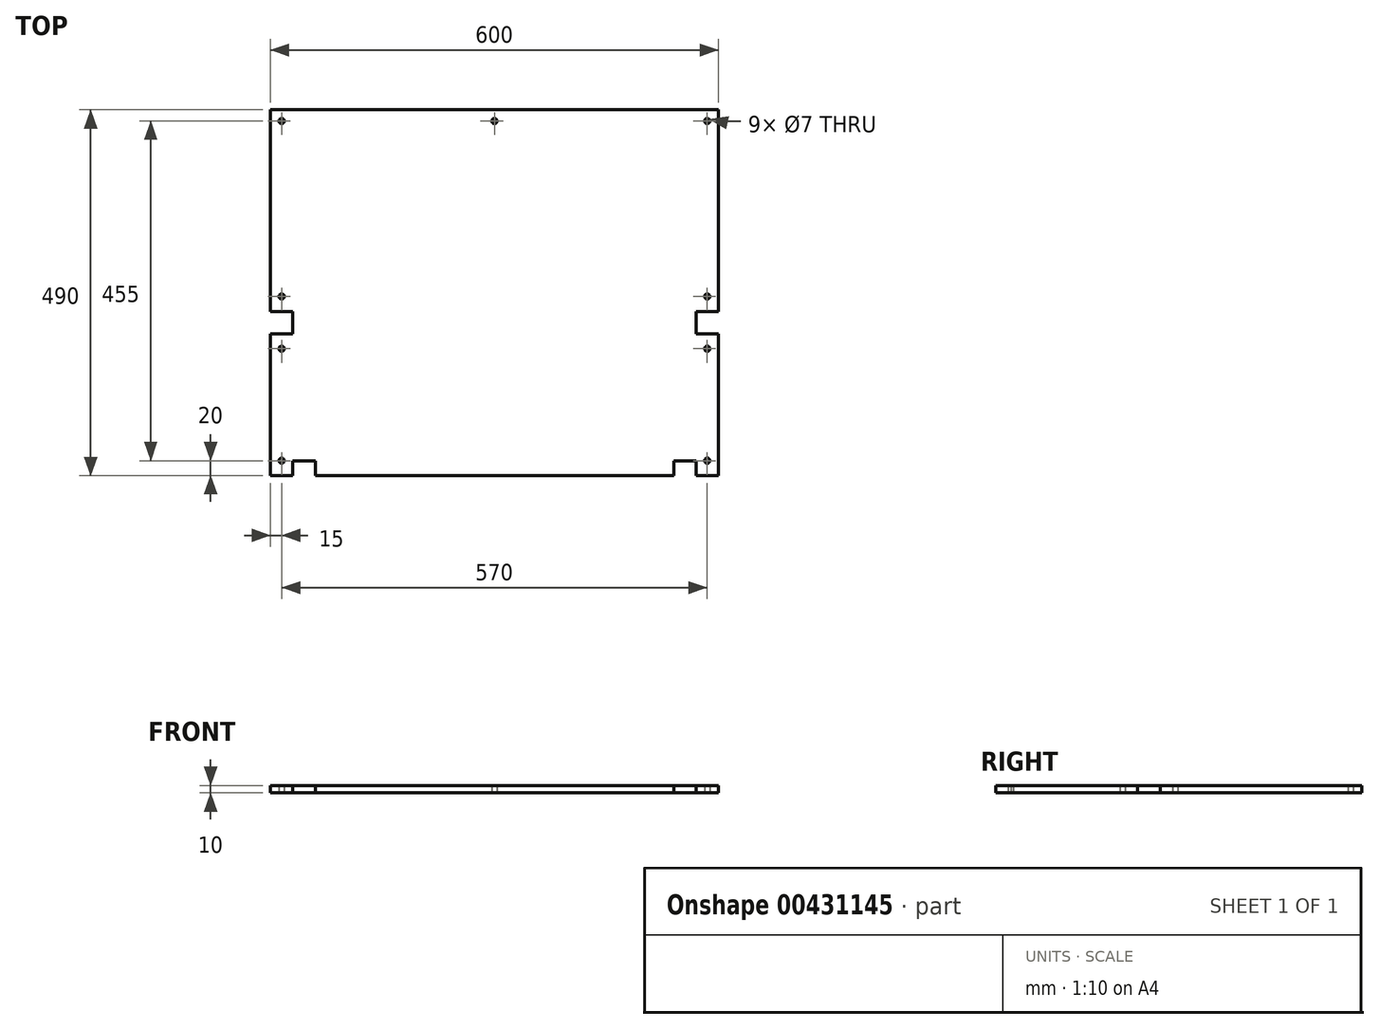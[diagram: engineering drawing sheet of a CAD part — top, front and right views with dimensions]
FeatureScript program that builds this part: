
annotation { "Feature Type Name" : "Feature", "Feature Type Description" : "" }
export const myFeature = defineFeature(function(context is Context, id is Id, definition is map)
    precondition{}
    {
        {
            var Q0;
            Q0=qCreatedBy(makeId("Top.planeOp"),FACE);
            var sketch = newSketch(context, id + "F0", { "sketchPlane" : qUnion([Q0])});
            skLineSegment(sketch, "E0.bottom", {"start": v(300, 245) * mm, "end": v(-300, 245) * mm});
            skLineSegment(sketch, "E0.top", {"start": v(300, -245) * mm, "end": v(-300, -245) * mm});
            skLineSegment(sketch, "E0.left", {"start": v(300, 245) * mm, "end": v(300, -245) * mm});
            skLineSegment(sketch, "E0.right", {"start": v(-300, 245) * mm, "end": v(-300, -245) * mm});
            skPoint(sketch, "E0.middle", {"position": v(0, 0) * mm});
            skLineSegment(sketch, "E1", {"start": v(0, 245) * mm, "end": v(0, -245) * mm, "construction": true});
            skLineSegment(sketch, "E2", {"start": v(-285, 245) * mm, "end": v(-285, -245) * mm, "construction": true});
            skLineSegment(sketch, "E3.bottom", {"start": v(-300, -25) * mm, "end": v(-270, -25) * mm});
            skLineSegment(sketch, "E3.top", {"start": v(-300, -55) * mm, "end": v(-270, -55) * mm});
            skLineSegment(sketch, "E3.left", {"start": v(-300, -25) * mm, "end": v(-300, -55) * mm});
            skLineSegment(sketch, "E3.right", {"start": v(-270, -25) * mm, "end": v(-270, -55) * mm});
            skCircle(sketch, "E4", {"center": v(-285, 230) * mm, "radius": 3.5 * mm});
            skCircle(sketch, "E5", {"center": v(-285, -5) * mm, "radius": 3.5 * mm});
            skPoint(sketch, "E6.centerSnap0", {"position": v(-270, -40) * mm});
            skCircle(sketch, "E7", {"center": v(-285, -75) * mm, "radius": 3.5 * mm});
            skCircle(sketch, "E8", {"center": v(-285, -225) * mm, "radius": 3.5 * mm});
            skCircle(sketch, "E9.MirrorC", {"center": v(285, 230) * mm, "radius": 3.5 * mm});
            skLineSegment(sketch, "E10.MirrorCS", {"start": v(300, -245) * mm, "end": v(270, -245) * mm});
            skCircle(sketch, "E11", {"center": v(0, 230) * mm, "radius": 3.5 * mm});
            skCircle(sketch, "E12.MirrorC", {"center": v(285, -5) * mm, "radius": 3.5 * mm});
            skLineSegment(sketch, "E13.MirrorCS", {"start": v(300, -25) * mm, "end": v(270, -25) * mm});
            skLineSegment(sketch, "E14.MirrorCS", {"start": v(270, -25) * mm, "end": v(270, -55) * mm});
            skLineSegment(sketch, "E15.MirrorCS", {"start": v(300, -55) * mm, "end": v(270, -55) * mm});
            skCircle(sketch, "E16.MirrorC", {"center": v(285, -75) * mm, "radius": 3.5 * mm});
            skCircle(sketch, "E17.MirrorC", {"center": v(285, -225) * mm, "radius": 3.5 * mm});
            skLineSegment(sketch, "E18", {"start": v(-270, -245) * mm, "end": v(-270, -225) * mm});
            skLineSegment(sketch, "E19", {"start": v(-270, -225) * mm, "end": v(-240, -225) * mm});
            skLineSegment(sketch, "E20", {"start": v(-240, -225) * mm, "end": v(-240, -245) * mm});
            skLineSegment(sketch, "E21.MirrorCS", {"start": v(270, -225) * mm, "end": v(240, -225) * mm});
            skLineSegment(sketch, "E22.MirrorCS", {"start": v(270, -245) * mm, "end": v(270, -225) * mm});
            skLineSegment(sketch, "E23.MirrorCS", {"start": v(240, -225) * mm, "end": v(240, -245) * mm});
            skSolve(sketch);
        }
        {
            var Q0;
            {var subQ5=sQuery(id+"F0.wireOp",EDGE,"E0.bottom");Q0=makeQuery(id+"F0.imprint","IMPRINT",FACE,{"disambiguationData":[TD([[makeQuery(id+"F0.imprint","IMPRINT",EDGE,{"derivedFrom":subQ5}),1.0]])]});}
            extrude(context, id + "F1", {"entities" : qUnion([Q0]), "depth" : 10 * mm});
        }
    });
